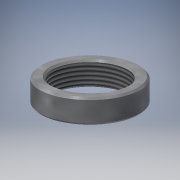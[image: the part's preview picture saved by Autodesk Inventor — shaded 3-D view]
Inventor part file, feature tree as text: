
AUTODESK INVENTOR PART (.ipt)
format: ipt  version: 2018 (Build 220112000, 112)  size: 137,216 bytes
history: native  units: mm
features: revolve x1, thread x1, sketch x1
ambient origin geometry x8: Origin, YZ Plane, XZ Plane, XY Plane, X Axis, Y Axis, Z Axis, Center Point
bodies: Solid1 (feature_tree)
feature tree (3):
  revolve  "Revolution1"  [1 undecoded]
  thread  "Thread1"  [1 undecoded]
  sketch  "Sketch1"  dims[d3=3.0mm d4=4.5mm d6=6.0mm d7=0.25mm d8=0.25mm d9=0.25mm d10=0.25mm d11=0.25mm d12=0.25mm d13=0.25mm d14=0.25mm d15=90.0deg d16=10.0mm d17=0.0mm]
note: 2 required parameter values undecoded (feature->parameter linkage not recoverable at this tier; creation-order binding heuristic only, values carry confidence <= 0.55)